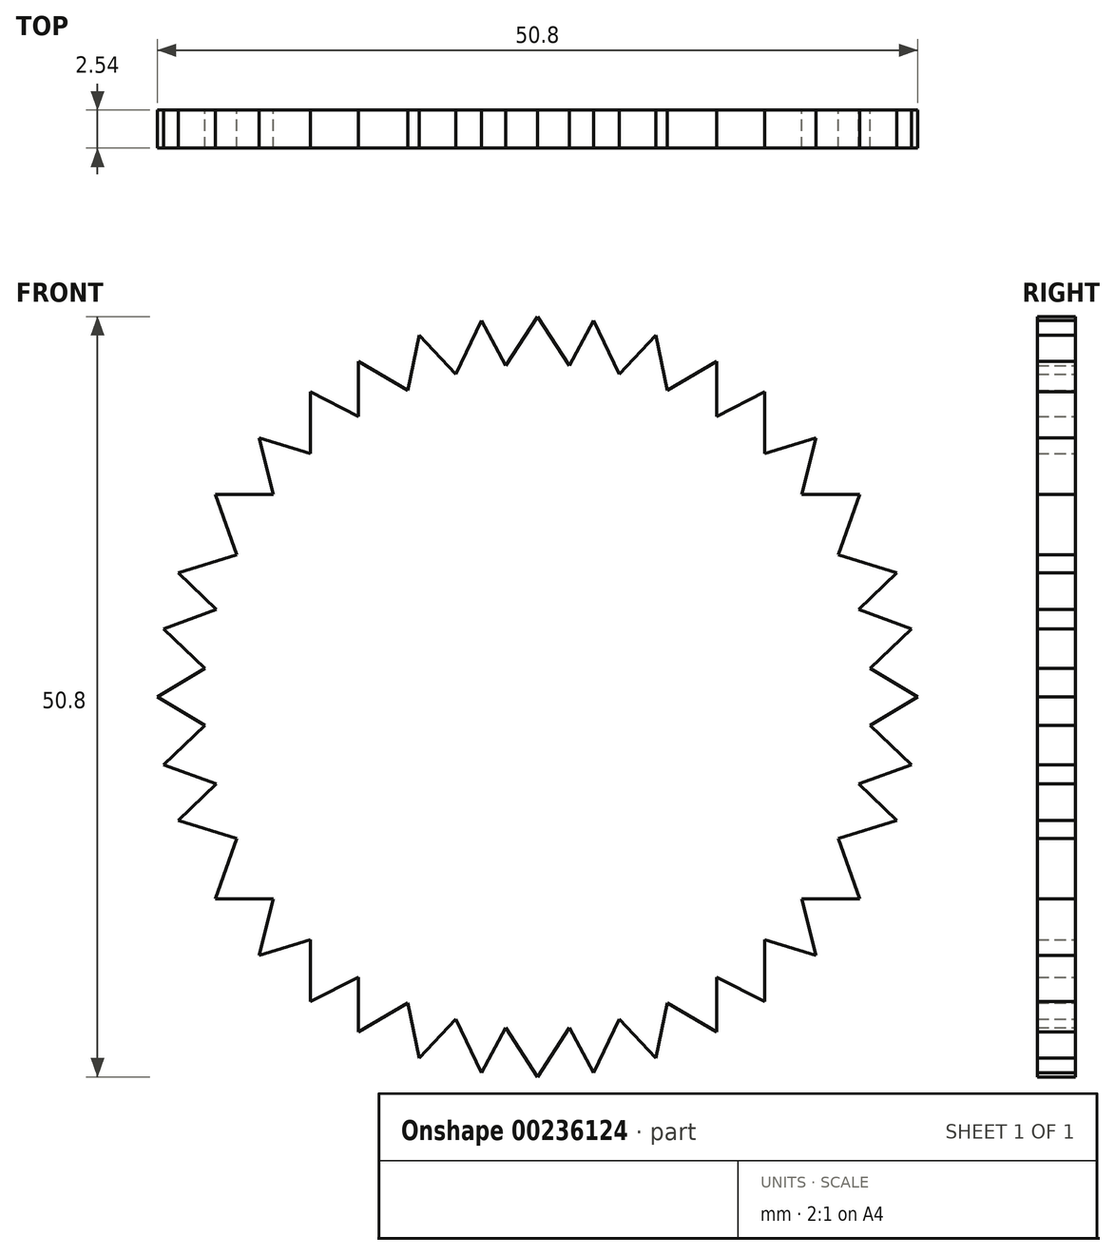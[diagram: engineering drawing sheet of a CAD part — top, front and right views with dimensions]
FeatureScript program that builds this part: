
annotation { "Feature Type Name" : "Feature", "Feature Type Description" : "" }
export const myFeature = defineFeature(function(context is Context, id is Id, definition is map)
    precondition{}
    {
        {
            var Q0;
            Q0=qCreatedBy(makeId("Front.planeOp"),FACE);
            var sketch = newSketch(context, id + "F0", { "sketchPlane" : qUnion([Q0])});
            skLineSegment(sketch, "E0", {"start": v(-2.02, 22.13) * mm, "end": v(0, 25.4) * mm});
            skLineSegment(sketch, "E1", {"start": v(0, 25.4) * mm, "end": v(2.11, 22.12) * mm});
            skLineSegment(sketch, "E2", {"start": v(2.11, 22.12) * mm, "end": v(3.75, 25.12) * mm});
            skLineSegment(sketch, "E3", {"start": v(3.75, 25.12) * mm, "end": v(5.47, 21.54) * mm});
            skLineSegment(sketch, "E4", {"start": v(5.47, 21.54) * mm, "end": v(7.92, 24.13) * mm});
            skLineSegment(sketch, "E5", {"start": v(7.92, 24.13) * mm, "end": v(8.65, 20.47) * mm});
            skLineSegment(sketch, "E6", {"start": v(8.65, 20.47) * mm, "end": v(11.96, 22.4) * mm});
            skLineSegment(sketch, "E7", {"start": v(11.96, 22.4) * mm, "end": v(11.96, 18.73) * mm});
            skLineSegment(sketch, "E8", {"start": v(11.96, 18.73) * mm, "end": v(15.16, 20.38) * mm});
            skLineSegment(sketch, "E9", {"start": v(15.16, 20.38) * mm, "end": v(15.16, 16.25) * mm});
            skLineSegment(sketch, "E10", {"start": v(15.16, 16.25) * mm, "end": v(18.6, 17.3) * mm});
            skLineSegment(sketch, "E11", {"start": v(18.6, 17.3) * mm, "end": v(17.65, 13.5) * mm});
            skLineSegment(sketch, "E12", {"start": v(17.65, 13.5) * mm, "end": v(21.52, 13.5) * mm});
            skLineSegment(sketch, "E13", {"start": v(21.52, 13.5) * mm, "end": v(20.1, 9.48) * mm});
            skLineSegment(sketch, "E14", {"start": v(20.1, 9.48) * mm, "end": v(24.02, 8.27) * mm});
            skLineSegment(sketch, "E15", {"start": v(24.02, 8.27) * mm, "end": v(21.45, 5.83) * mm});
            skLineSegment(sketch, "E16", {"start": v(21.45, 5.83) * mm, "end": v(25, 4.54) * mm});
            skLineSegment(sketch, "E17", {"start": v(25, 4.54) * mm, "end": v(22.15, 1.84) * mm});
            skLineSegment(sketch, "E18", {"start": v(22.15, 1.84) * mm, "end": v(25.4, 0) * mm});
            skLineSegment(sketch, "E19", {"start": v(25.4, 0) * mm, "end": v(22.14, -1.95) * mm});
            skLineSegment(sketch, "E20.MirrorCS", {"start": v(-20.1, 9.48) * mm, "end": v(-24.02, 8.27) * mm});
            skLineSegment(sketch, "E21.MirrorCS", {"start": v(-21.45, 5.83) * mm, "end": v(-25, 4.54) * mm});
            skLineSegment(sketch, "E22.MirrorCS", {"start": v(-22.15, 1.84) * mm, "end": v(-25.4, 0) * mm});
            skLineSegment(sketch, "E23.MirrorCS", {"start": v(-25.4, 0) * mm, "end": v(-22.14, -1.95) * mm});
            skLineSegment(sketch, "E24.MirrorCS", {"start": v(-15.16, 16.25) * mm, "end": v(-18.6, 17.3) * mm});
            skLineSegment(sketch, "E25.MirrorCS", {"start": v(-25, 4.54) * mm, "end": v(-22.15, 1.84) * mm});
            skLineSegment(sketch, "E26.MirrorCS", {"start": v(-24.02, 8.27) * mm, "end": v(-21.45, 5.83) * mm});
            skLineSegment(sketch, "E27.MirrorCS", {"start": v(-15.16, 20.38) * mm, "end": v(-15.16, 16.25) * mm});
            skLineSegment(sketch, "E28.MirrorCS", {"start": v(-18.6, 17.3) * mm, "end": v(-17.65, 13.5) * mm});
            skLineSegment(sketch, "E29.MirrorCS", {"start": v(-17.65, 13.5) * mm, "end": v(-21.52, 13.5) * mm});
            skLineSegment(sketch, "E30.MirrorCS", {"start": v(-11.96, 18.73) * mm, "end": v(-15.16, 20.38) * mm});
            skLineSegment(sketch, "E31.MirrorCS", {"start": v(-11.96, 22.4) * mm, "end": v(-11.96, 18.73) * mm});
            skLineSegment(sketch, "E32.MirrorCS", {"start": v(-8.65, 20.47) * mm, "end": v(-11.96, 22.4) * mm});
            skLineSegment(sketch, "E33.MirrorCS", {"start": v(2.02, 22.13) * mm, "end": v(0, 25.4) * mm});
            skLineSegment(sketch, "E34.MirrorCS", {"start": v(0, 25.4) * mm, "end": v(-2.11, 22.12) * mm});
            skLineSegment(sketch, "E35.MirrorCS", {"start": v(-7.92, 24.13) * mm, "end": v(-8.65, 20.47) * mm});
            skLineSegment(sketch, "E36.MirrorCS", {"start": v(-21.52, 13.5) * mm, "end": v(-20.1, 9.48) * mm});
            skLineSegment(sketch, "E37.MirrorCS", {"start": v(-5.47, 21.54) * mm, "end": v(-7.92, 24.13) * mm});
            skLineSegment(sketch, "E38.MirrorCS", {"start": v(-3.75, 25.12) * mm, "end": v(-5.47, 21.54) * mm});
            skLineSegment(sketch, "E39.MirrorCS", {"start": v(-2.11, 22.12) * mm, "end": v(-3.75, 25.12) * mm});
            skLineSegment(sketch, "E40.MirrorCS", {"start": v(2.02, -22.13) * mm, "end": v(0, -25.4) * mm});
            skLineSegment(sketch, "E41.MirrorCS", {"start": v(-15.16, -16.25) * mm, "end": v(-18.6, -17.3) * mm});
            skLineSegment(sketch, "E42.MirrorCS", {"start": v(15.16, -16.25) * mm, "end": v(18.6, -17.3) * mm});
            skLineSegment(sketch, "E43.MirrorCS", {"start": v(-2.02, -22.13) * mm, "end": v(0, -25.4) * mm});
            skLineSegment(sketch, "E44.MirrorCS", {"start": v(21.45, -5.83) * mm, "end": v(25, -4.54) * mm});
            skLineSegment(sketch, "E45.MirrorCS", {"start": v(-25.4, 0) * mm, "end": v(-22.14, 1.95) * mm});
            skLineSegment(sketch, "E46.MirrorCS", {"start": v(-5.47, -21.54) * mm, "end": v(-7.92, -24.13) * mm});
            skLineSegment(sketch, "E47.MirrorCS", {"start": v(7.92, -24.13) * mm, "end": v(8.65, -20.47) * mm});
            skLineSegment(sketch, "E48.MirrorCS", {"start": v(18.6, -17.3) * mm, "end": v(17.65, -13.5) * mm});
            skLineSegment(sketch, "E49.MirrorCS", {"start": v(15.16, -20.38) * mm, "end": v(15.16, -16.25) * mm});
            skLineSegment(sketch, "E50.MirrorCS", {"start": v(11.96, -18.73) * mm, "end": v(15.16, -20.38) * mm});
            skLineSegment(sketch, "E51.MirrorCS", {"start": v(-17.65, -13.5) * mm, "end": v(-21.52, -13.5) * mm});
            skLineSegment(sketch, "E52.MirrorCS", {"start": v(2.11, -22.12) * mm, "end": v(3.75, -25.12) * mm});
            skLineSegment(sketch, "E53.MirrorCS", {"start": v(0, -25.4) * mm, "end": v(2.11, -22.12) * mm});
            skLineSegment(sketch, "E54.MirrorCS", {"start": v(11.96, -22.4) * mm, "end": v(11.96, -18.73) * mm});
            skLineSegment(sketch, "E55.MirrorCS", {"start": v(-21.52, -13.5) * mm, "end": v(-20.1, -9.48) * mm});
            skLineSegment(sketch, "E56.MirrorCS", {"start": v(5.47, -21.54) * mm, "end": v(7.92, -24.13) * mm});
            skLineSegment(sketch, "E57.MirrorCS", {"start": v(8.65, -20.47) * mm, "end": v(11.96, -22.4) * mm});
            skLineSegment(sketch, "E58.MirrorCS", {"start": v(-24.02, -8.27) * mm, "end": v(-21.45, -5.83) * mm});
            skLineSegment(sketch, "E59.MirrorCS", {"start": v(-20.1, -9.48) * mm, "end": v(-24.02, -8.27) * mm});
            skLineSegment(sketch, "E60.MirrorCS", {"start": v(25, -4.54) * mm, "end": v(22.15, -1.84) * mm});
            skLineSegment(sketch, "E61.MirrorCS", {"start": v(-8.65, -20.47) * mm, "end": v(-11.96, -22.4) * mm});
            skLineSegment(sketch, "E62.MirrorCS", {"start": v(22.15, -1.84) * mm, "end": v(25.4, 0) * mm});
            skLineSegment(sketch, "E63.MirrorCS", {"start": v(-3.75, -25.12) * mm, "end": v(-5.47, -21.54) * mm});
            skLineSegment(sketch, "E64.MirrorCS", {"start": v(3.75, -25.12) * mm, "end": v(5.47, -21.54) * mm});
            skLineSegment(sketch, "E65.MirrorCS", {"start": v(0, -25.4) * mm, "end": v(-2.11, -22.12) * mm});
            skLineSegment(sketch, "E66.MirrorCS", {"start": v(25.4, 0) * mm, "end": v(22.14, 1.95) * mm});
            skLineSegment(sketch, "E67.MirrorCS", {"start": v(-2.11, -22.12) * mm, "end": v(-3.75, -25.12) * mm});
            skLineSegment(sketch, "E68.MirrorCS", {"start": v(-18.6, -17.3) * mm, "end": v(-17.65, -13.5) * mm});
            skLineSegment(sketch, "E69.MirrorCS", {"start": v(-22.15, -1.84) * mm, "end": v(-25.4, 0) * mm});
            skLineSegment(sketch, "E70.MirrorCS", {"start": v(-11.96, -22.4) * mm, "end": v(-11.96, -18.73) * mm});
            skLineSegment(sketch, "E71.MirrorCS", {"start": v(17.65, -13.5) * mm, "end": v(21.52, -13.5) * mm});
            skLineSegment(sketch, "E72.MirrorCS", {"start": v(24.02, -8.27) * mm, "end": v(21.45, -5.83) * mm});
            skLineSegment(sketch, "E73.MirrorCS", {"start": v(-11.96, -18.73) * mm, "end": v(-15.16, -20.38) * mm});
            skLineSegment(sketch, "E74.MirrorCS", {"start": v(-7.92, -24.13) * mm, "end": v(-8.65, -20.47) * mm});
            skLineSegment(sketch, "E75.MirrorCS", {"start": v(-21.45, -5.83) * mm, "end": v(-25, -4.54) * mm});
            skLineSegment(sketch, "E76.MirrorCS", {"start": v(20.1, -9.48) * mm, "end": v(24.02, -8.27) * mm});
            skLineSegment(sketch, "E77.MirrorCS", {"start": v(-15.16, -20.38) * mm, "end": v(-15.16, -16.25) * mm});
            skLineSegment(sketch, "E78.MirrorCS", {"start": v(-25, -4.54) * mm, "end": v(-22.15, -1.84) * mm});
            skLineSegment(sketch, "E79.MirrorCS", {"start": v(21.52, -13.5) * mm, "end": v(20.1, -9.48) * mm});
            skSolve(sketch);
        }
        {
            var Q0;
            Q0 = qSketchRegion(id + "F0", true);
            var Q1;
            Q1=makeQuery(id+"F0.imprint","IMPRINT",FACE,{"disambiguationData":[TD([[makeQuery(id+"F0.imprint","IMPRINT",EDGE,{"derivedFrom":sQuery(id+"F0.wireOp",EDGE,"E6")}),-1.0]])]});
            extrude(context, id + "F1", {"entities" : qUnion([Q0, Q1]), "depth" : 2.54 * mm});
        }
    });
